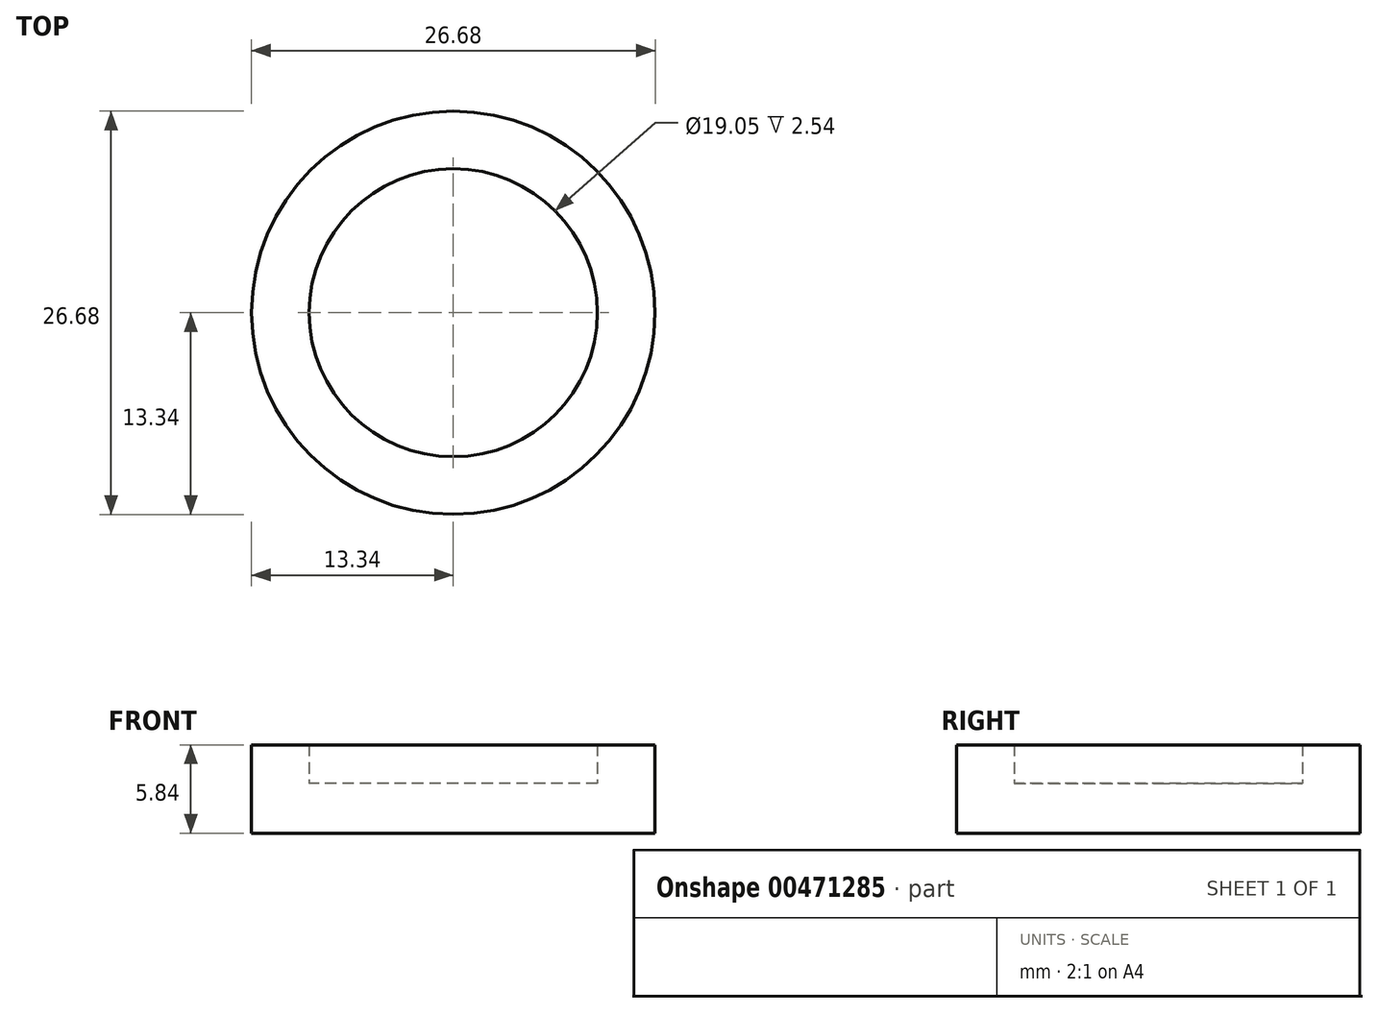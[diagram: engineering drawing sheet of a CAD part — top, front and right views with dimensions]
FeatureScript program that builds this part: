
annotation { "Feature Type Name" : "Feature", "Feature Type Description" : "" }
export const myFeature = defineFeature(function(context is Context, id is Id, definition is map)
    precondition{}
    {
        {
            var Q0;
            Q0=qCreatedBy(makeId("Top.planeOp"),FACE);
            var sketch = newSketch(context, id + "F0", { "sketchPlane" : qUnion([Q0])});
            skCircle(sketch, "E0", {"center": v(0, 0) * mm, "radius": 9.53 * mm});
            skCircle(sketch, "E1.0", {"center": v(0, 0) * mm, "radius": 13.33 * mm});
            skSolve(sketch);
        }
        {
            var Q0;
            Q0=makeQuery(id+"F0.imprint","IMPRINT",FACE,{"disambiguationData":[TD([[makeQuery(id+"F0.imprint","IMPRINT",EDGE,{"derivedFrom":sQuery(id+"F0.wireOp",EDGE,"E0")}),-1.0]])]});
            var Q1;
            Q1=makeQuery(id+"F0.imprint","IMPRINT",FACE,{"disambiguationData":[TD([[makeQuery(id+"F0.imprint","IMPRINT",EDGE,{"derivedFrom":sQuery(id+"F0.wireOp",EDGE,"E0")}),1.0]])]});
            extrude(context, id + "F1", {"entities" : qUnion([Q0, Q1]), "oppositeDirection" : true, "depth" : 3.3 * mm, "offsetDistance" : 25.4 * mm});
        }
        {
            var Q0;
            Q0 = qSketchRegion(id + "F0", true);
            extrude(context, id + "F2", {"entities" : qUnion([Q0]), "operationType" : NewBodyOperationType.ADD, "depth" : 2.54 * mm, "offsetDistance" : 25.4 * mm});
        }
    });
